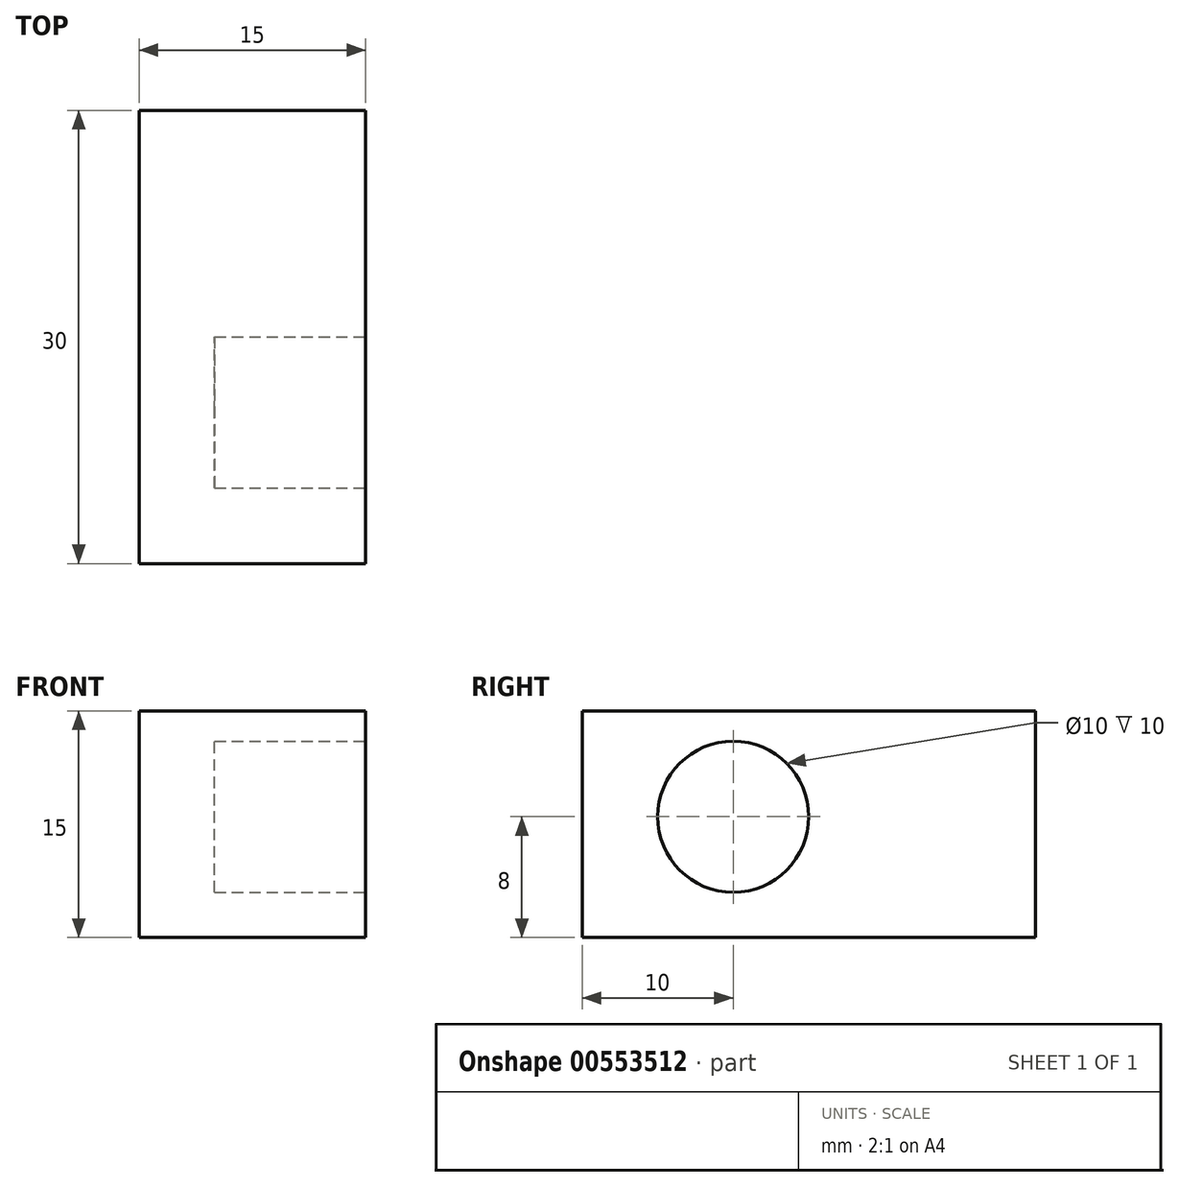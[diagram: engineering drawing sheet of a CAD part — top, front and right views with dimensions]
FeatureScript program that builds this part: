
annotation { "Feature Type Name" : "Feature", "Feature Type Description" : "" }
export const myFeature = defineFeature(function(context is Context, id is Id, definition is map)
    precondition{}
    {
        {
            var Q0;
            Q0=qCreatedBy(makeId("Front.planeOp"),FACE);
            var sketch = newSketch(context, id + "F0", { "sketchPlane" : qUnion([Q0])});
            skLineSegment(sketch, "E0.bottom", {"start": v(0, 0) * mm, "end": v(15, 0) * mm});
            skLineSegment(sketch, "E0.top", {"start": v(0, 15) * mm, "end": v(15, 15) * mm});
            skLineSegment(sketch, "E0.left", {"start": v(0, 0) * mm, "end": v(0, 15) * mm});
            skLineSegment(sketch, "E0.right", {"start": v(15, 0) * mm, "end": v(15, 15) * mm});
            skSolve(sketch);
        }
        {
            var Q0;
            Q0=makeQuery(id+"F0.imprint","IMPRINT",FACE,{"disambiguationData":[TD([[makeQuery(id+"F0.imprint","IMPRINT",EDGE,{"derivedFrom":sQuery(id+"F0.wireOp",EDGE,"E0.bottom")}),1.0]])]});
            extrude(context, id + "F1", {"entities" : qUnion([Q0]), "depth" : 30 * mm, "offsetDistance" : 25 * mm});
        }
        {
            var Q0;
            Q0=makeQuery(id+"F1.opExtrude","SWEPT_FACE",FACE,{"disambiguationData":[OSD([sQuery(id+"F0.wireOp",EDGE,"E0.right")])]});
            var sketch = newSketch(context, id + "F2", { "sketchPlane" : qUnion([Q0])});
            skCircle(sketch, "E1", {"center": v(-20, 8) * mm, "radius": 5 * mm});
            skSolve(sketch);
        }
        {
            var Q0;
            Q0=makeQuery(id+"F2.imprint","IMPRINT",FACE,{"disambiguationData":[TD([[makeQuery(id+"F2.imprint","IMPRINT",EDGE,{"derivedFrom":sQuery(id+"F2.wireOp",EDGE,"E1")}),1.0]])]});
            extrude(context, id + "F3", {"entities" : qUnion([Q0]), "operationType" : NewBodyOperationType.REMOVE, "oppositeDirection" : true, "depth" : 10 * mm, "offsetDistance" : 25 * mm});
        }
    });
